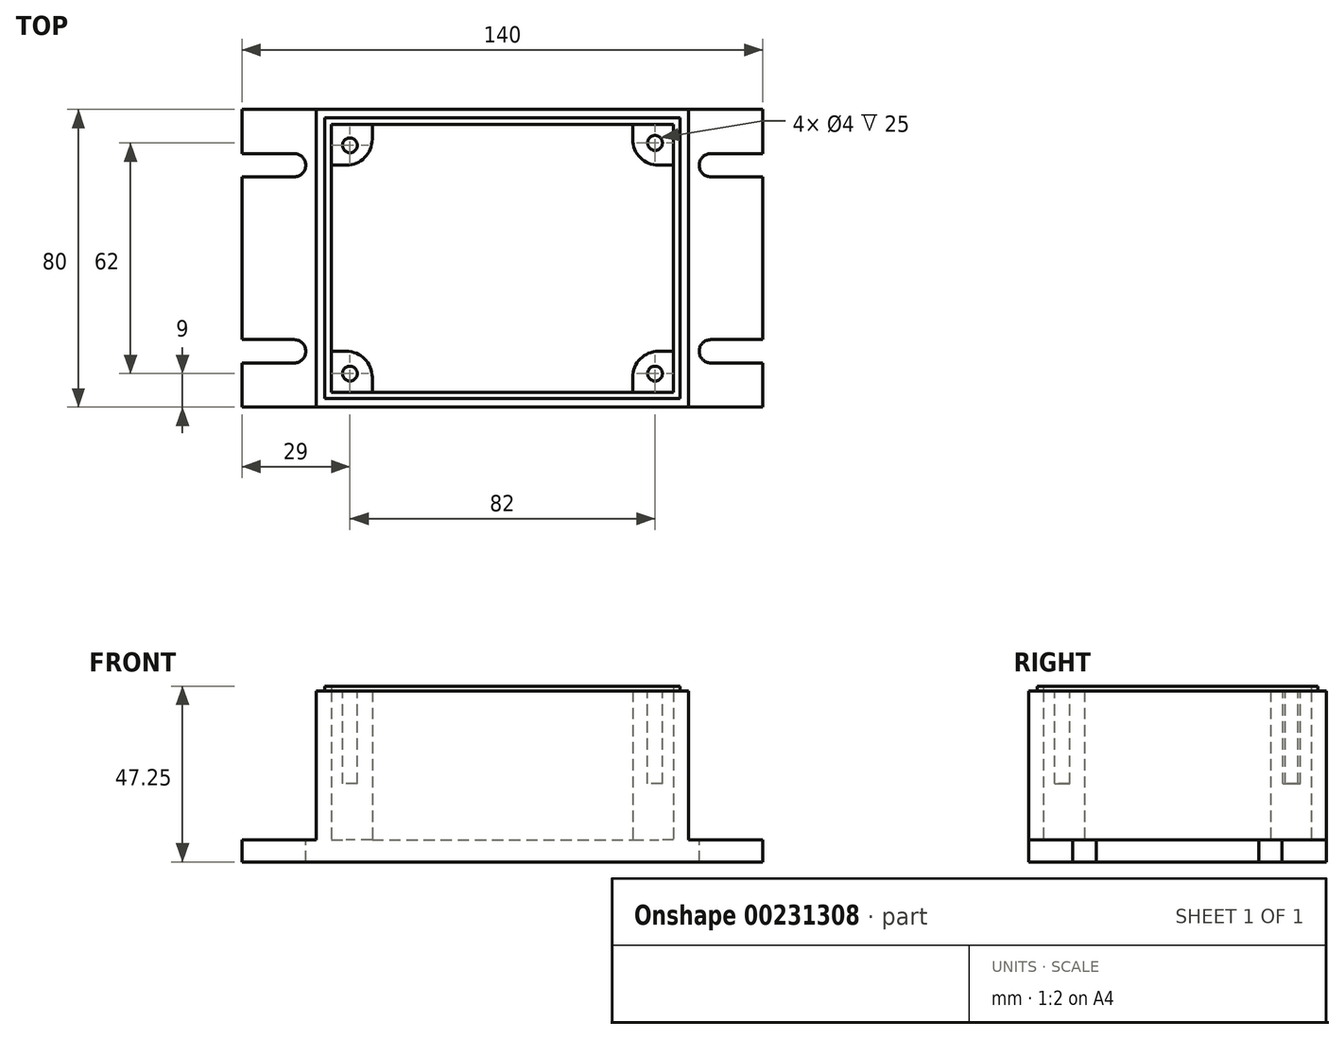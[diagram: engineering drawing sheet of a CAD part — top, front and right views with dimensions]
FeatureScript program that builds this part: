
annotation { "Feature Type Name" : "Feature", "Feature Type Description" : "" }
export const myFeature = defineFeature(function(context is Context, id is Id, definition is map)
    precondition{}
    {
        {
            var Q0;
            Q0=qCreatedBy(makeId("Top.planeOp"),FACE);
            var sketch = newSketch(context, id + "F0", { "sketchPlane" : qUnion([Q0])});
            skLineSegment(sketch, "E0.bottom", {"start": v(0, 0) * mm, "end": v(100, 0) * mm});
            skLineSegment(sketch, "E0.top", {"start": v(0, 80) * mm, "end": v(100, 80) * mm});
            skLineSegment(sketch, "E0.left", {"start": v(0, 0) * mm, "end": v(0, 80) * mm});
            skLineSegment(sketch, "E0.right", {"start": v(100, 0) * mm, "end": v(100, 80) * mm});
            skLineSegment(sketch, "E1.bottom", {"start": v(15, 4) * mm, "end": v(85, 4) * mm});
            skLineSegment(sketch, "E1.top", {"start": v(15, 76) * mm, "end": v(85, 76) * mm});
            skLineSegment(sketch, "E1.left", {"start": v(4, 15) * mm, "end": v(4, 65) * mm});
            skLineSegment(sketch, "E1.right", {"start": v(96, 15) * mm, "end": v(96, 65) * mm});
            skLineSegment(sketch, "E2.top", {"start": v(4, 65) * mm, "end": v(15, 65) * mm});
            skLineSegment(sketch, "E2.right", {"start": v(15, 76) * mm, "end": v(15, 65) * mm});
            skLineSegment(sketch, "E3.top", {"start": v(4, 15) * mm, "end": v(15, 15) * mm});
            skLineSegment(sketch, "E3.right", {"start": v(15, 4) * mm, "end": v(15, 15) * mm});
            skLineSegment(sketch, "E4.top", {"start": v(96, 15) * mm, "end": v(85, 15) * mm});
            skLineSegment(sketch, "E4.right", {"start": v(85, 4) * mm, "end": v(85, 15) * mm});
            skLineSegment(sketch, "E5.top", {"start": v(96, 65) * mm, "end": v(85, 65) * mm});
            skLineSegment(sketch, "E5.right", {"start": v(85, 76) * mm, "end": v(85, 65) * mm});
            skSolve(sketch);
        }
        {
            var Q0;
            Q0 = qSketchRegion(id + "F0", true);
            extrude(context, id + "F1", {"entities" : qUnion([Q0]), "depth" : 40 * mm});
        }
        {
            var Q0;
            Q0=makeQuery(id+"F1.opExtrude","CAP_FACE",FACE,{"disambiguationData":[OSD([sQuery(id+"F0.wireOp",EDGE,"E0.bottom"),sQuery(id+"F0.wireOp",EDGE,"E0.top"),sQuery(id+"F0.wireOp",EDGE,"E0.left"),sQuery(id+"F0.wireOp",EDGE,"E0.right"),sQuery(id+"F0.wireOp",EDGE,"E1.bottom"),sQuery(id+"F0.wireOp",EDGE,"E1.top"),sQuery(id+"F0.wireOp",EDGE,"E1.left"),sQuery(id+"F0.wireOp",EDGE,"E1.right")])],"isStart":true});
            var sketch = newSketch(context, id + "F2", { "sketchPlane" : qUnion([Q0])});
            skLineSegment(sketch, "E6.bottom", {"start": v(-20, 0) * mm, "end": v(120, 0) * mm});
            skLineSegment(sketch, "E6.top", {"start": v(-20, -80) * mm, "end": v(120, -80) * mm});
            skLineSegment(sketch, "E6.left", {"start": v(-20, 0) * mm, "end": v(-20, -11.88) * mm});
            skLineSegment(sketch, "E6.right", {"start": v(120, 0) * mm, "end": v(120, -11.88) * mm});
            skArc(sketch, "E7", {"start": v(-6, -68.13) * mm, "mid": v(-2.88, -65) * mm, "end": v(-6, -61.88) * mm});
            skArc(sketch, "E8", {"start": v(-6, -18.13) * mm, "mid": v(-2.87, -15) * mm, "end": v(-6, -11.88) * mm});
            skArc(sketch, "E9", {"start": v(106, -11.88) * mm, "mid": v(102.88, -15) * mm, "end": v(106, -18.12) * mm});
            skArc(sketch, "E10", {"start": v(106, -61.88) * mm, "mid": v(102.88, -65) * mm, "end": v(106, -68.12) * mm});
            skLineSegment(sketch, "E11", {"start": v(-6, -68.13) * mm, "end": v(-20, -68.13) * mm});
            skLineSegment(sketch, "E12", {"start": v(-6, -61.88) * mm, "end": v(-20, -61.88) * mm});
            skLineSegment(sketch, "E13.trimOffspring", {"start": v(-20, -68.13) * mm, "end": v(-20, -80) * mm});
            skLineSegment(sketch, "E14.bottom", {"start": v(-6, -18.13) * mm, "end": v(-20, -18.13) * mm});
            skLineSegment(sketch, "E14.top", {"start": v(-6, -11.88) * mm, "end": v(-20, -11.88) * mm});
            skLineSegment(sketch, "E15.bottom", {"start": v(106, -18.12) * mm, "end": v(120, -18.12) * mm});
            skLineSegment(sketch, "E15.top", {"start": v(106, -11.88) * mm, "end": v(120, -11.88) * mm});
            skLineSegment(sketch, "E16.bottom", {"start": v(106, -68.12) * mm, "end": v(120, -68.12) * mm});
            skLineSegment(sketch, "E16.top", {"start": v(106, -61.88) * mm, "end": v(120, -61.88) * mm});
            skLineSegment(sketch, "E17.trimOffspring", {"start": v(-20, -18.13) * mm, "end": v(-20, -61.88) * mm});
            skLineSegment(sketch, "E18.trimOffspring", {"start": v(120, -18.12) * mm, "end": v(120, -61.88) * mm});
            skLineSegment(sketch, "E19.trimOffspring", {"start": v(120, -68.12) * mm, "end": v(120, -80) * mm});
            skSolve(sketch);
        }
        {
            var Q0;
            Q0 = qSketchRegion(id + "F2", true);
            extrude(context, id + "F3", {"entities" : qUnion([Q0]), "operationType" : NewBodyOperationType.ADD, "depth" : 6 * mm});
        }
        {
            var Q0;
            Q0=makeQuery(id+"F1.opExtrude","SWEPT_EDGE",EDGE,{"disambiguationData":[OSD([sQuery(id+"F0.wireOp",EDGE,"E2.top"),sQuery(id+"F0.wireOp",EDGE,"E2.right")])]});
            var Q1;
            Q1=makeQuery(id+"F1.opExtrude","SWEPT_EDGE",EDGE,{"disambiguationData":[OSD([sQuery(id+"F0.wireOp",EDGE,"E3.top"),sQuery(id+"F0.wireOp",EDGE,"E3.right")])]});
            var Q2;
            Q2=makeQuery(id+"F1.opExtrude","SWEPT_EDGE",EDGE,{"disambiguationData":[OSD([sQuery(id+"F0.wireOp",EDGE,"E5.top"),sQuery(id+"F0.wireOp",EDGE,"E5.right")])]});
            var Q3;
            Q3=makeQuery(id+"F1.opExtrude","SWEPT_EDGE",EDGE,{"disambiguationData":[OSD([sQuery(id+"F0.wireOp",EDGE,"E4.top"),sQuery(id+"F0.wireOp",EDGE,"E4.right")])]});
            fillet(context, id + "F4", {"entities" : qUnion([Q0, Q1, Q2, Q3]), "radius" : 7 * mm, "tangentPropagation" : true, "allowEdgeOverflow" : false});
        }
        {
            var Q0;
            Q0=makeQuery(id+"F1.opExtrude","CAP_FACE",FACE,{"disambiguationData":[OSD([sQuery(id+"F0.wireOp",EDGE,"E0.bottom"),sQuery(id+"F0.wireOp",EDGE,"E0.top"),sQuery(id+"F0.wireOp",EDGE,"E0.left"),sQuery(id+"F0.wireOp",EDGE,"E0.right"),sQuery(id+"F0.wireOp",EDGE,"E1.bottom"),sQuery(id+"F0.wireOp",EDGE,"E1.top"),sQuery(id+"F0.wireOp",EDGE,"E1.left"),sQuery(id+"F0.wireOp",EDGE,"E1.right"),sQuery(id+"F0.wireOp",EDGE,"E2.top"),sQuery(id+"F0.wireOp",EDGE,"E2.right"),sQuery(id+"F0.wireOp",EDGE,"E3.top"),sQuery(id+"F0.wireOp",EDGE,"E3.right"),sQuery(id+"F0.wireOp",EDGE,"E4.top"),sQuery(id+"F0.wireOp",EDGE,"E4.right"),sQuery(id+"F0.wireOp",EDGE,"E5.top"),sQuery(id+"F0.wireOp",EDGE,"E5.right")])],"isStart":false});
            var sketch = newSketch(context, id + "F5", { "sketchPlane" : qUnion([Q0])});
            skLineSegment(sketch, "E20.bottom", {"start": v(2.25, 77.75) * mm, "end": v(97.75, 77.75) * mm});
            skLineSegment(sketch, "E20.top", {"start": v(2.25, 2.25) * mm, "end": v(97.75, 2.25) * mm});
            skLineSegment(sketch, "E20.left", {"start": v(2.25, 77.75) * mm, "end": v(2.25, 2.25) * mm});
            skLineSegment(sketch, "E20.right", {"start": v(97.75, 77.75) * mm, "end": v(97.75, 2.25) * mm});
            skLineSegment(sketch, "E21.bottom", {"start": v(4, 76) * mm, "end": v(96, 76) * mm});
            skLineSegment(sketch, "E21.top", {"start": v(4, 4) * mm, "end": v(96, 4) * mm});
            skLineSegment(sketch, "E21.left", {"start": v(4, 76) * mm, "end": v(4, 4) * mm});
            skLineSegment(sketch, "E21.right", {"start": v(96, 76) * mm, "end": v(96, 4) * mm});
            skSolve(sketch);
        }
        {
            var Q0;
            Q0 = qSketchRegion(id + "F5", true);
            extrude(context, id + "F6", {"entities" : qUnion([Q0]), "operationType" : NewBodyOperationType.ADD, "depth" : 1.25 * mm});
        }
        {
            var Q0;
            {var subQ0=sQuery(id+"F0.wireOp",EDGE,"E1.left");var subQ1=sQuery(id+"F0.wireOp",EDGE,"E3.right");var subQ2=sQuery(id+"F0.wireOp",EDGE,"E3.top");var subQ3=sQuery(id+"F0.wireOp",EDGE,"E1.bottom");Q0=makeQuery(id+"F6.boolean.opBoolean","SPLIT",FACE,{"disambiguationData":[TD([makeQuery(id+"F1.opExtrude","SWEPT_FACE",FACE,{"disambiguationData":[OSD([subQ2])]})])],"derivedFrom":makeQuery(id+"F1.opExtrude","CAP_FACE",FACE,{"disambiguationData":[OSD([sQuery(id+"F0.wireOp",EDGE,"E0.bottom"),sQuery(id+"F0.wireOp",EDGE,"E0.top"),sQuery(id+"F0.wireOp",EDGE,"E0.left"),sQuery(id+"F0.wireOp",EDGE,"E0.right"),subQ3,sQuery(id+"F0.wireOp",EDGE,"E1.top"),subQ0,sQuery(id+"F0.wireOp",EDGE,"E1.right"),sQuery(id+"F0.wireOp",EDGE,"E2.top"),sQuery(id+"F0.wireOp",EDGE,"E2.right"),subQ2,subQ1,sQuery(id+"F0.wireOp",EDGE,"E4.top"),sQuery(id+"F0.wireOp",EDGE,"E4.right"),sQuery(id+"F0.wireOp",EDGE,"E5.top"),sQuery(id+"F0.wireOp",EDGE,"E5.right")])],"isStart":false})});}
            var sketch = newSketch(context, id + "F7", { "sketchPlane" : qUnion([Q0])});
            skCircle(sketch, "E22", {"center": v(9, 9) * mm, "radius": 2 * mm});
            skCircle(sketch, "E23", {"center": v(9, 70.34) * mm, "radius": 2 * mm});
            skCircle(sketch, "E24", {"center": v(91, 71) * mm, "radius": 2 * mm});
            skCircle(sketch, "E25", {"center": v(91, 9) * mm, "radius": 2 * mm});
            skSolve(sketch);
        }
        {
            var Q0;
            Q0 = qSketchRegion(id + "F7", true);
            extrude(context, id + "F8", {"entities" : qUnion([Q0]), "operationType" : NewBodyOperationType.REMOVE, "oppositeDirection" : true, "depth" : 25 * mm});
        }
    });
